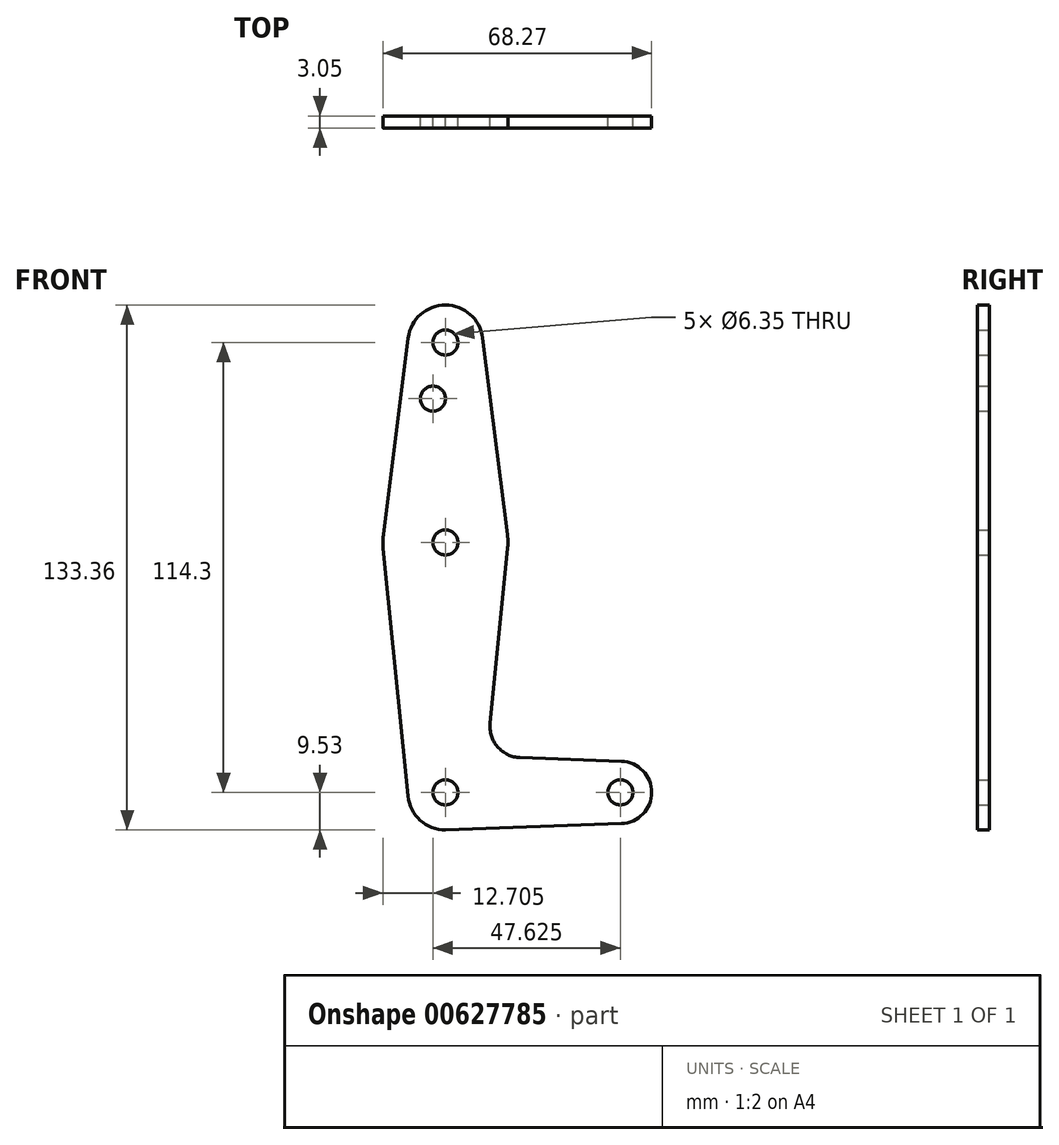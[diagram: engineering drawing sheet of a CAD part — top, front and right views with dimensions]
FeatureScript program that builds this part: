
annotation { "Feature Type Name" : "Feature", "Feature Type Description" : "" }
export const myFeature = defineFeature(function(context is Context, id is Id, definition is map)
    precondition{}
    {
        {
            var Q0;
            Q0=qCreatedBy(makeId("Front.planeOp"),FACE);
            var sketch = newSketch(context, id + "F0", { "sketchPlane" : qUnion([Q0])});
            skArc(sketch, "E0", {"start": v(-9.48, -0.95) * mm, "mid": v(-6.13, -7.29) * mm, "end": v(0.68, -9.5) * mm});
            skArc(sketch, "E1", {"start": v(9.45, 115.5) * mm, "mid": v(0, 123.83) * mm, "end": v(-9.45, 115.5) * mm});
            skArc(sketch, "E2", {"start": v(44.73, -7.93) * mm, "mid": v(52.39, 0) * mm, "end": v(44.73, 7.93) * mm});
            skLineSegment(sketch, "E3", {"start": v(9.45, 115.5) * mm, "end": v(15.75, 65.48) * mm});
            skLineSegment(sketch, "E4", {"start": v(-9.45, 115.5) * mm, "end": v(-15.75, 65.48) * mm});
            skLineSegment(sketch, "E5", {"start": v(-15.8, 61.91) * mm, "end": v(-9.48, -0.95) * mm});
            skLineSegment(sketch, "E6", {"start": v(15.8, 61.91) * mm, "end": v(11.34, 17.59) * mm});
            skLineSegment(sketch, "E7", {"start": v(0, -9.53) * mm, "end": v(44.73, -7.93) * mm});
            skLineSegment(sketch, "E8", {"start": v(18.97, 8.85) * mm, "end": v(44.73, 7.93) * mm});
            skCircle(sketch, "E9", {"center": v(0, 114.3) * mm, "radius": 3.18 * mm});
            skCircle(sketch, "E10", {"center": v(0, 63.5) * mm, "radius": 3.18 * mm});
            skCircle(sketch, "E11", {"center": v(0, 0) * mm, "radius": 3.18 * mm});
            skCircle(sketch, "E12", {"center": v(44.45, 0) * mm, "radius": 3.18 * mm});
            skCircle(sketch, "E13", {"center": v(-3.17, 100.03) * mm, "radius": 3.18 * mm});
            skPoint(sketch, "E14.newPointA", {"position": v(9.57, 0) * mm});
            skPoint(sketch, "E14.newPointB", {"position": v(0, 9.53) * mm});
            skPoint(sketch, "E15.orphan", {"position": v(-9.57, 0) * mm});
            skPoint(sketch, "E16.visualSharp", {"position": v(10.5, 9.15) * mm});
            skArc(sketch, "E16.filletArc", {"start": v(11.34, 17.59) * mm, "mid": v(13.26, 11.57) * mm, "end": v(18.97, 8.85) * mm});
            skArc(sketch, "E17", {"start": v(15.8, 61.91) * mm, "mid": v(15.87, 63.7) * mm, "end": v(15.75, 65.48) * mm});
            skArc(sketch, "E18", {"start": v(-15.75, 65.48) * mm, "mid": v(-15.87, 63.7) * mm, "end": v(-15.8, 61.91) * mm});
            skSolve(sketch);
        }
        {
            var Q0;
            {var subQ0=sQuery(id+"F0.wireOp",EDGE,"E7");var subQ1=sQuery(id+"F0.wireOp",EDGE,"E0");var subQ2=makeQuery(id+"F0.imprint","INTERSECT",VERTEX,{"disambiguationData":[OD(0.0)],"derivedFrom":[subQ1,subQ0]});Q0=makeQuery(id+"F0.imprint","IMPRINT",FACE,{"disambiguationData":[TD([[makeQuery(id+"F0.imprint","IMPRINT",EDGE,{"disambiguationData":[TD([[subQ2,1.0]])],"derivedFrom":subQ1}),1.0]])]});}
            var Q1;
            Q1=makeQuery(id+"F0.imprint","IMPRINT",FACE,{"disambiguationData":[TD([[makeQuery(id+"F0.imprint","IMPRINT",EDGE,{"derivedFrom":sQuery(id+"F0.wireOp",EDGE,"E1")}),1.0]])]});
            extrude(context, id + "F1", {"entities" : qUnion([Q0, Q1]), "depth" : 3.05 * mm, "offsetDistance" : 25.4 * mm});
        }
    });
